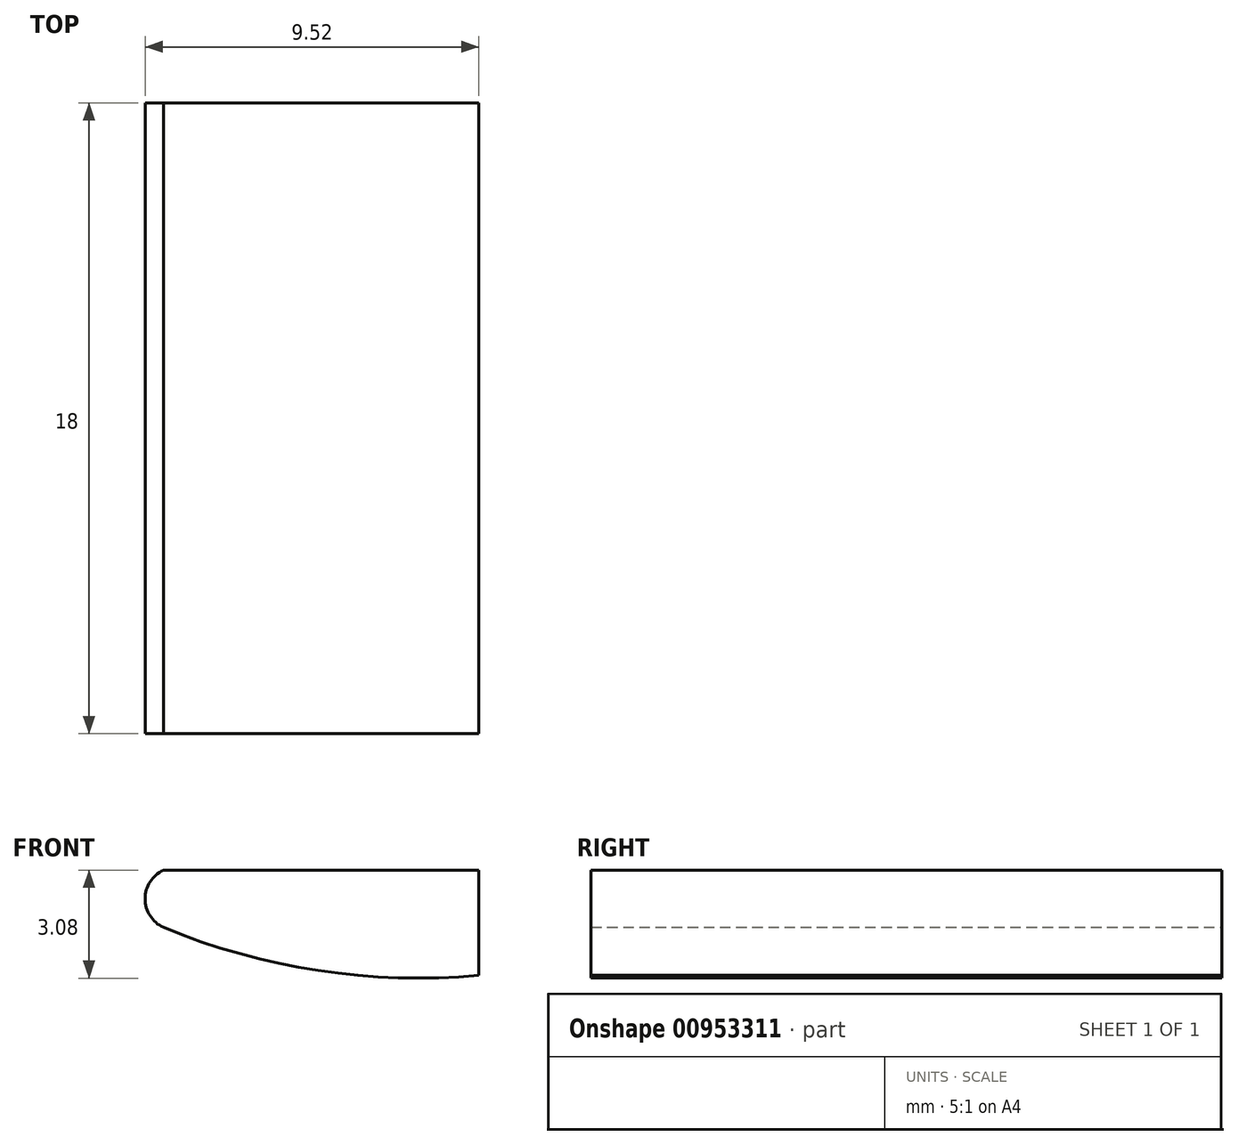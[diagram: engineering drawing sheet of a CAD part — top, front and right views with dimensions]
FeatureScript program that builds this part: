
annotation { "Feature Type Name" : "Feature", "Feature Type Description" : "" }
export const myFeature = defineFeature(function(context is Context, id is Id, definition is map)
    precondition{}
    {
        {
            var Q0;
            Q0=qCreatedBy(makeId("Front.planeOp"),FACE);
            var sketch = newSketch(context, id + "F0", { "sketchPlane" : qUnion([Q0])});
            skLineSegment(sketch, "E0", {"start": v(0, 0) * mm, "end": v(0, 3) * mm});
            skLineSegment(sketch, "E1", {"start": v(0, 3) * mm, "end": v(-9, 3) * mm});
            skArc(sketch, "E2", {"start": v(-9, 1.37) * mm, "mid": v(-4.58, 0.14) * mm, "end": v(0, 0) * mm});
            skArc(sketch, "E3", {"start": v(-9, 3) * mm, "mid": v(-9.52, 2.18) * mm, "end": v(-9, 1.37) * mm});
            skSolve(sketch);
        }
        {
            var Q0;
            Q0=makeQuery(id+"F0.imprint","IMPRINT",FACE,{"disambiguationData":[TD([[makeQuery(id+"F0.imprint","IMPRINT",EDGE,{"derivedFrom":sQuery(id+"F0.wireOp",EDGE,"E0")}),1.0]])]});
            extrude(context, id + "F1", {"entities" : qUnion([Q0]), "depth" : 60 * mm, "offsetDistance" : 25 * mm});
        }
        {
            var Q0;
            Q0=makeQuery(id+"F1.opExtrude","CAP_FACE",FACE,{"disambiguationData":[OSD([sQuery(id+"F0.wireOp",EDGE,"E0"),sQuery(id+"F0.wireOp",EDGE,"E1"),sQuery(id+"F0.wireOp",EDGE,"E2"),sQuery(id+"F0.wireOp",EDGE,"E3")])],"isStart":false});
            extrude(context, id + "F2", {"entities" : qUnion([Q0]), "operationType" : NewBodyOperationType.ADD, "depth" : -42 * mm, "offsetDistance" : 25 * mm});
        }
        {
            var Q0;
            Q0=makeQuery(id+"F1.opExtrude","CAP_FACE",FACE,{"disambiguationData":[OSD([sQuery(id+"F0.wireOp",EDGE,"E0"),sQuery(id+"F0.wireOp",EDGE,"E1"),sQuery(id+"F0.wireOp",EDGE,"E2"),sQuery(id+"F0.wireOp",EDGE,"E3")])],"isStart":false});
            extrude(context, id + "F3", {"entities" : qUnion([Q0]), "operationType" : NewBodyOperationType.REMOVE, "oppositeDirection" : true, "depth" : 42 * mm, "offsetDistance" : 25 * mm});
        }
    });
